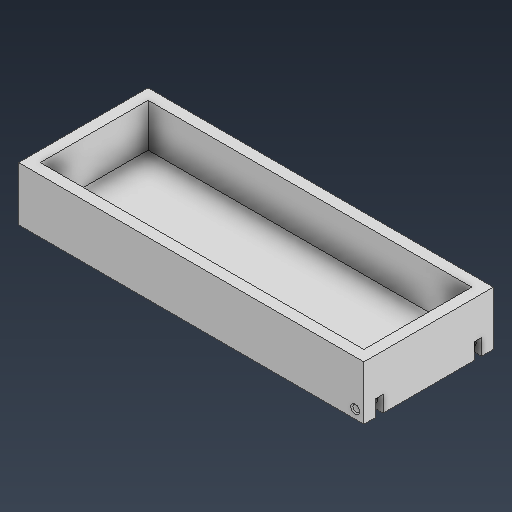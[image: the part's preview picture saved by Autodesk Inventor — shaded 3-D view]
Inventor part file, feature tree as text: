
AUTODESK INVENTOR PART (.ipt)
format: ipt  version: 2021 (Build 250183000, 183)  size: 192,512 bytes
history: native  units: in
note: dims shown in document units (in); Inventor stores cm internally (conversion verified against a paired STEP export)
features: extrude x7, sketch x6, fillet x1, plane x1
ambient origin geometry x8: Origin, YZ Plane, XZ Plane, XY Plane, X Axis, Y Axis, Z Axis, Center Point
bodies: Solid1 (feature_tree)
feature tree (15):
  sketch  "Sketch1"  dims[d0=3.937in d1=11.811in]
  extrude  "Extrusion1"  Depth=11.811in
  extrude  "Extrusion2"  Depth=0.3937in TaperAngle=0.0deg
  extrude  "Extrusion3"  Depth=1.9685in
  fillet  "Fillet1"  Radius=0.1378in
  extrude  "Extrusion4"  TaperAngle=135.0deg  [1 undecoded]
  plane  "Work Plane1"
  extrude  "Extrusion5"  Depth=5.9055in TaperAngle=0.0deg
  extrude  "Extrusion6"  Depth=0.4331in
  extrude  "Extrusion7"  Depth=0.2677in
  sketch  "Sketch2"  dims[d2=0.3937in d3=0.3937in d4=0.0in]
  sketch  "Sketch3"  dims[d5=1.9685in d6=0.0in d7=0.1378in d8=0.1378in]
  sketch  "Sketch4"  dims[d9=0.25in d10=135.0deg]
  sketch  "Sketch5"  dims[d11=0.25in d12=5.9055in d13=0.0in]
  sketch  "Sketch6"  dims[d14=0.0394in d15=0.4331in d16=0.2677in d17=0.5906in d18=0.4331in d19=0.2677in d20=0.5118in d21=0.0in d22=0.3071in d23=0.0531in d24=0.0157in d25=0.0157in d26=3.3228in d27=0.0in d28=0.1181in d29=3.3228in d30=0.0in d31=0.1181in d32=3.3228in d33=0.0in]
note: 1 required parameter value undecoded (feature->parameter linkage not recoverable at this tier; creation-order binding heuristic only, values carry confidence <= 0.55)
